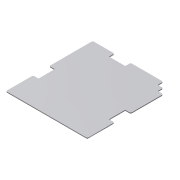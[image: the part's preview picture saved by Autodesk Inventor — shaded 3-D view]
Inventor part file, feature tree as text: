
AUTODESK INVENTOR PART (.ipt)
format: ipt  version: 2014 (Build 180170000, 170)  size: 152,064 bytes
history: native  units: mm
features: extrude x3, sketch x3, fillet x1
ambient origin geometry x8: Origin, YZ Plane, XZ Plane, XY Plane, X Axis, Y Axis, Z Axis, Center Point
bodies: Solid1 (feature_tree)
feature tree (7):
  extrude  "Extrusion1"  Depth=400.0mm
  extrude  "Extrusion6"  Depth=25.0mm
  extrude  "Extrusion7"  Depth=200.0mm
  fillet  "Fillet3"  Radius=200.0mm
  sketch  "Sketch1"  dims[d0=375.0mm d1=400.0mm]
  sketch  "Sketch6"  dims[d2=4.0mm d3=0.0mm d22=25.0mm]
  sketch  "Sketch7"  dims[d23=4.0mm d24=0.0mm d25=200.0mm d26=200.0mm d28=4.0mm d29=0.0mm d30=6.0mm]
